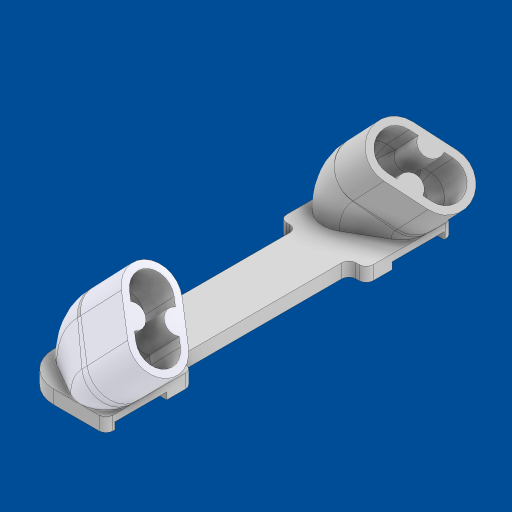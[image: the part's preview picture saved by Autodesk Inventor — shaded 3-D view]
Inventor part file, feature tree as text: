
AUTODESK INVENTOR PART (.ipt)
format: ipt  version: 2023 (Build 270158000, 158)  size: 665,088 bytes
history: native  units: mm
features: extrude x17, sketch x12, fillet x3, plane x2, revolve x2, chamfer x2, sweep x1, mirror x1
ambient origin geometry x8: Origin, YZ Plane, XZ Plane, XY Plane, X Axis, Y Axis, Z Axis, Center Point
bodies: Solid1 (feature_tree)
feature tree (40):
  sketch  "Sketch1"  dims[d0=100.0mm d1=25.0mm d2=7.5mm d3=7.5mm d4=60.0deg d5=15.0mm d6=11.0mm d7=11.0mm d8=15.0mm d11=135.0deg]
  plane  "Work Plane1"
  sweep  "Sweep1"
  extrude  "Extrusion1"  Depth=4.0mm TaperAngle=0.0deg
  revolve  "Revolution1"  Angle=45.0deg
  sketch  "Sketch6"  dims[d31=10.0mm d32=45.0deg]
  extrude  "Extrusion4"  TaperAngle=45.0deg  [1 undecoded]
  extrude  "Extrusion5"  Depth=10.0mm
  sketch  "Sketch7"  dims[d33=10.0mm d34=10.0mm]
  extrude  "Extrusion6"  Depth=10.0mm
  extrude  "Extrusion7"  Depth=15.0mm
  mirror  "Mirror4"
  plane  "Work Plane9"
  extrude  "Extrusion8"  Depth=5.5mm
  revolve  "Revolution2"  [1 undecoded]
  extrude  "Extrusion9"  Depth=2.0mm
  sketch  "Sketch19"  dims[d60=5.5mm d61=5.5mm]
  extrude  "Extrusion10"  Depth=15.0mm TaperAngle=0.0deg
  extrude  "Extrusion11"  Depth=7.5mm
  extrude  "Extrusion12"  TaperAngle=90.0deg  [1 undecoded]
  sketch  "Sketch21"  dims[d65=2.0mm d66=6.5mm]
  extrude  "Extrusion13"  Depth=7.5mm
  chamfer  "Chamfer3"  Distance=5.5mm
  extrude  "Extrusion15"  Depth=2.0mm
  extrude  "Extrusion18"  Depth=2.0mm
  fillet  "Fillet2"  Radius=11.0mm
  fillet  "Fillet3"  Radius=11.0mm
  extrude  "Extrusion19"  Depth=2.0mm
  extrude  "Extrusion20"  Depth=2.0mm
  sketch  "Sketch22"  dims[d67=6.5mm d68=15.0mm d69=0.0mm]
  extrude  "Extrusion22"  Depth=2.0mm
  chamfer  "Chamfer6"  Distance=10.0mm
  extrude  "Extrusion23"  Depth=10.0mm TaperAngle=0.0deg
  fillet  "Fillet4"  Radius=20.0mm
  sketch  "Sketch3"  dims[d12=0.0mm d13=0.0mm d14=4.0mm d15=0.0mm]
  sketch  "Sketch5"  dims[d29=11.389087mm d30=45.0deg]
  sketch  "Sketch14"  dims[d35=45.0deg d37=10.0mm]
  sketch  "Sketch15"  dims[d38=0.977384mm d57=15.0mm]
  sketch  "Sketch20"  dims[d63=11.0mm d64=11.0mm]
  sketch  "Sketch23"  dims[d70=325.0mm d71=0.0mm d72=7.5mm d73=90.0deg d74=7.5mm d75=5.5mm d76=5.5mm d77=15.0mm d78=11.0mm d79=11.0mm d80=2.0mm d81=6.5mm d82=6.5mm d83=10.0mm d84=0.0mm d93=10.0mm d94=0.0mm d115=20.0mm d116=0.0mm d131=8.726646mm d132=300.0mm d133=0.0mm d134=15.0mm d135=300.0mm d136=0.0mm d137=11.0mm d138=11.0mm d139=2.0mm d140=6.5mm d141=6.5mm d142=10.0mm d143=0.0mm d144=40.0mm d145=0.0mm d146=25.0mm d147=100.0mm d150=15.0mm d151=5.5mm d152=2.0mm d153=0.0mm d156=2.0mm d157=4.0mm d158=45.0deg d162=549.891mm d163=50.0mm d164=100.0mm d167=2.5mm d169=15.0mm d170=17.5mm d171=17.5mm d174=10.0mm d175=300.0mm d176=0.0mm d177=7.5mm d183=2.0mm d184=0.0mm d185=2.0mm d186=10.0mm d187=3.0mm d188=0.0mm d189=15.0mm d190=0.0mm d193=6.5mm d194=5.0mm d195=0.0mm d199=2.0mm d200=4.0mm d201=45.0deg d202=5.0mm d203=50.0mm d204=10.0mm d205=0.0mm d206=2.0mm d178=0.872665mm d196=0.5mm d197=0.872665mm]
note: 3 required parameter values undecoded (feature->parameter linkage not recoverable at this tier; creation-order binding heuristic only, values carry confidence <= 0.55)